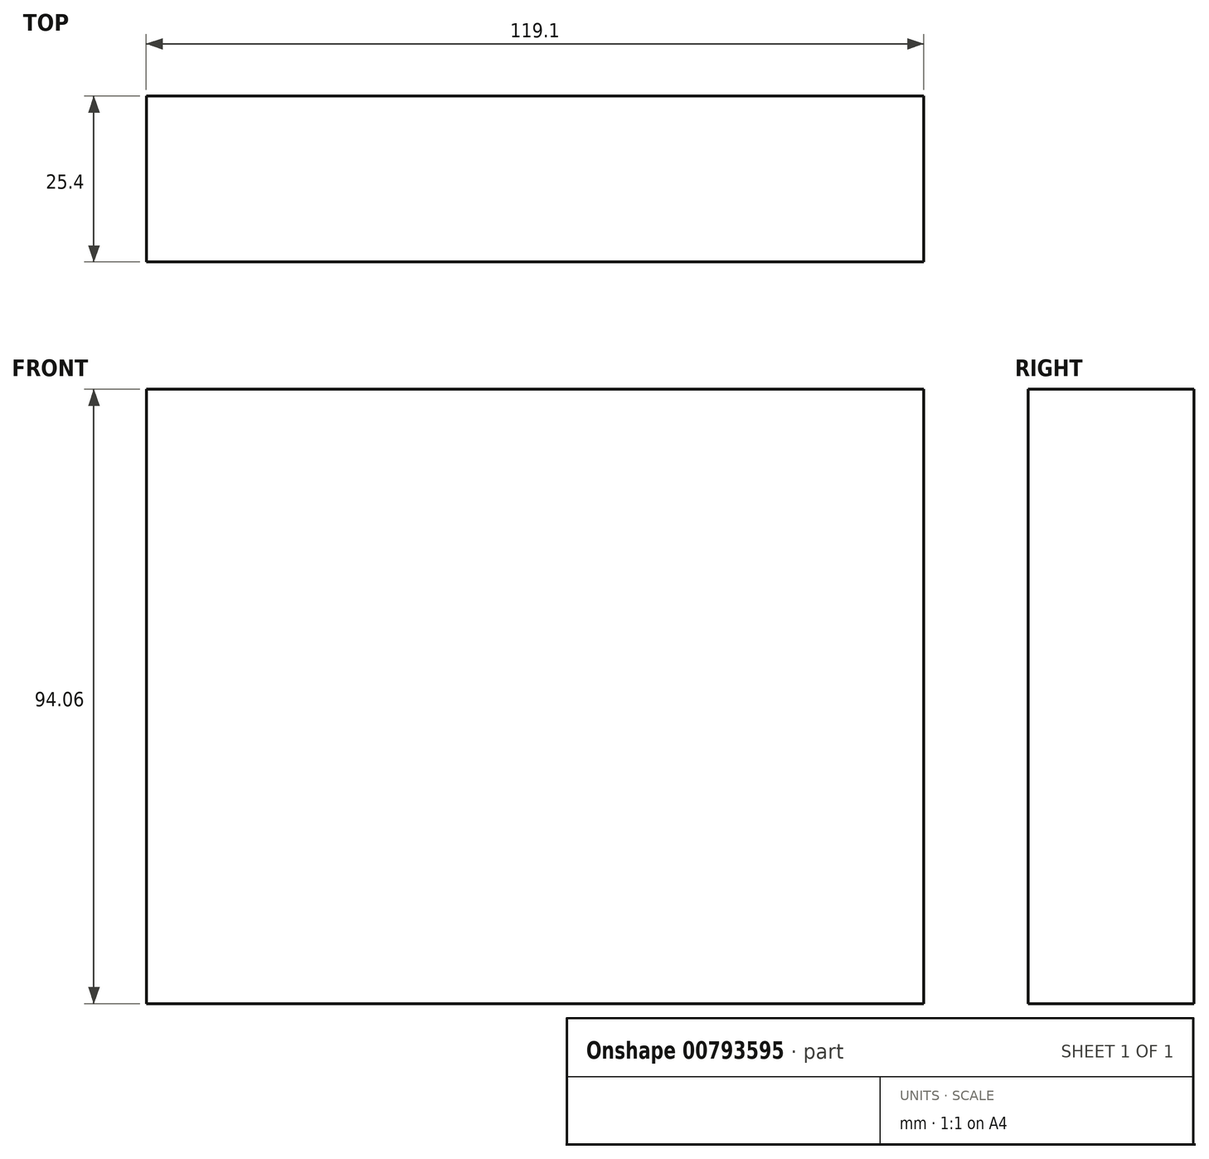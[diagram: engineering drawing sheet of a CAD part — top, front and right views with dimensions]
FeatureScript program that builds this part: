
annotation { "Feature Type Name" : "Feature", "Feature Type Description" : "" }
export const myFeature = defineFeature(function(context is Context, id is Id, definition is map)
    precondition{}
    {
        {
            var Q0;
            Q0=qCreatedBy(makeId("Front.planeOp"),FACE);
            var sketch = newSketch(context, id + "F0", { "sketchPlane" : qUnion([Q0])});
            skLineSegment(sketch, "E0.bottom", {"start": v(-54.2, 46.57) * mm, "end": v(64.9, 46.57) * mm});
            skLineSegment(sketch, "E0.top", {"start": v(-54.2, -47.49) * mm, "end": v(64.9, -47.49) * mm});
            skLineSegment(sketch, "E0.left", {"start": v(-54.2, 46.57) * mm, "end": v(-54.2, -47.49) * mm});
            skLineSegment(sketch, "E0.right", {"start": v(64.9, 46.57) * mm, "end": v(64.9, -47.49) * mm});
            skSolve(sketch);
        }
        {
            var Q0;
            Q0 = qSketchRegion(id + "F0", true);
            extrude(context, id + "F1", {"entities" : qUnion([Q0]), "depth" : 25.4 * mm, "offsetDistance" : 25.4 * mm});
        }
    });
